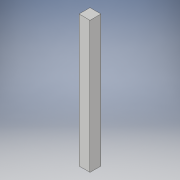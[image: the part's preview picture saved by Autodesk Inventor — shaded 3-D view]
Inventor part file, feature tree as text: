
AUTODESK INVENTOR PART (.ipt)
format: ipt  version: 2017 (Build 210142000, 142)  size: 90,624 bytes
history: native  units: in
note: dims shown in document units (in); Inventor stores cm internally (conversion verified against a paired STEP export)
features: extrude x1, sketch x1
ambient origin geometry x8: Origin, YZ Plane, XZ Plane, XY Plane, X Axis, Y Axis, Z Axis, Center Point
bodies: Solid1 (feature_tree)
feature tree (2):
  extrude  "Extrusion1"  Depth=2.0in
  sketch  "Sketch1"  dims[d0=24.0in d1=2.0in d2=2.0in d3=0.0in]
